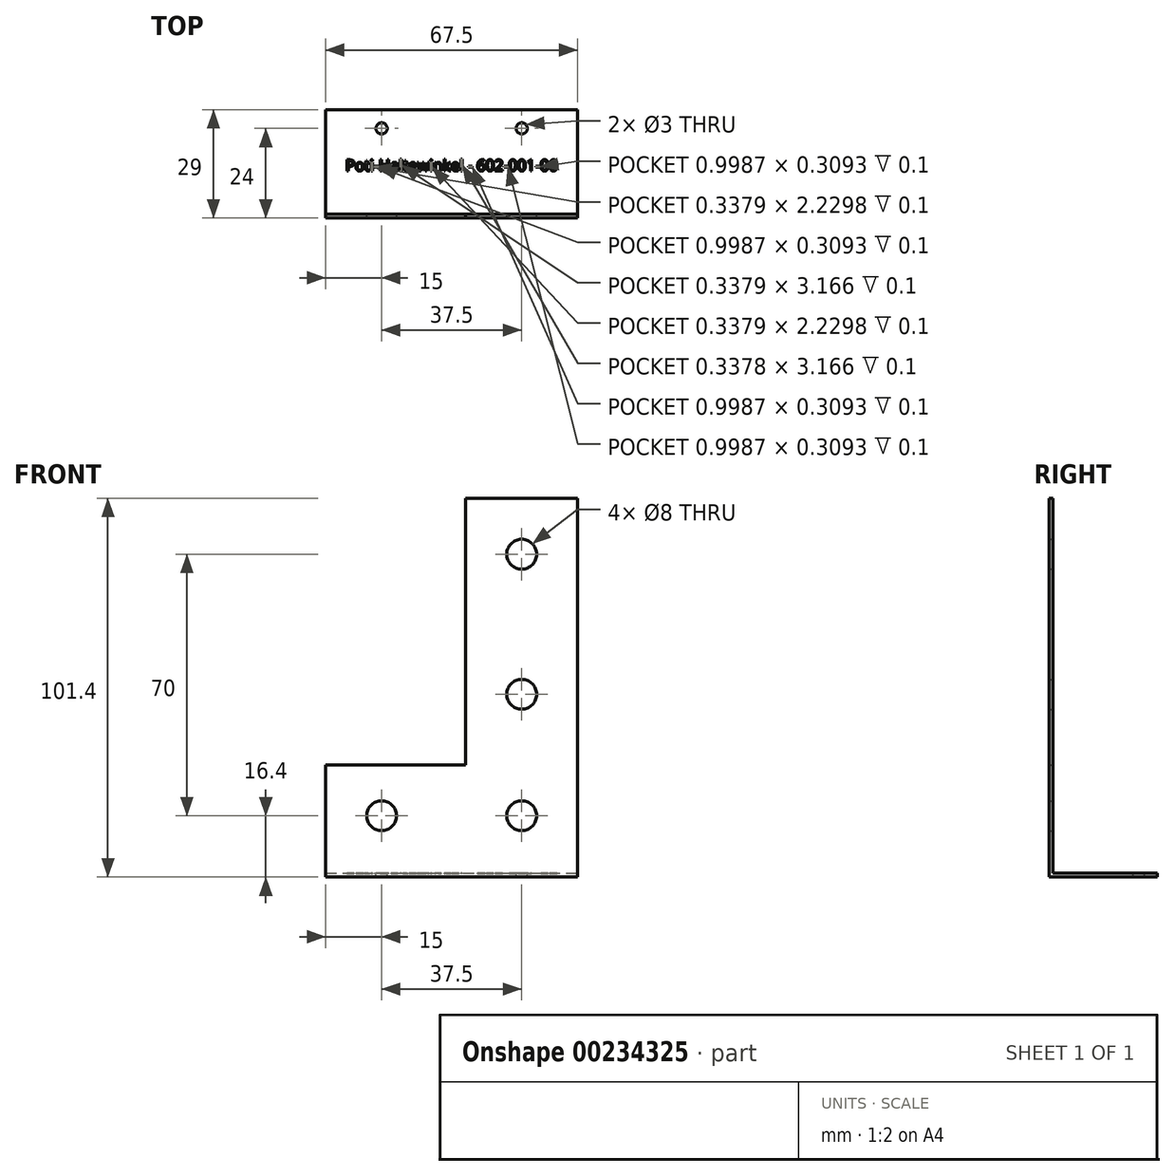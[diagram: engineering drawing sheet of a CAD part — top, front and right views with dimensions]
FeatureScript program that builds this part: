
annotation { "Feature Type Name" : "Feature", "Feature Type Description" : "" }
export const myFeature = defineFeature(function(context is Context, id is Id, definition is map)
    precondition{}
    {
        {
            var Q0;
            Q0=qCreatedBy(makeId("Front.planeOp"),FACE);
            var sketch = newSketch(context, id + "F0", { "sketchPlane" : qUnion([Q0])});
            skLineSegment(sketch, "E0", {"start": v(-37.5, 0) * mm, "end": v(0, 0) * mm});
            skLineSegment(sketch, "E1", {"start": v(0, 0) * mm, "end": v(0, 71.4) * mm});
            skLineSegment(sketch, "E2", {"start": v(0, 71.4) * mm, "end": v(30, 71.4) * mm});
            skLineSegment(sketch, "E3", {"start": v(30, 71.4) * mm, "end": v(30, -30) * mm});
            skLineSegment(sketch, "E4", {"start": v(30, -30) * mm, "end": v(-37.5, -30) * mm});
            skLineSegment(sketch, "E5", {"start": v(-37.5, -30) * mm, "end": v(-37.5, 0) * mm});
            skCircle(sketch, "E6", {"center": v(15, 56.4) * mm, "radius": 4 * mm});
            skPoint(sketch, "E6.centerSnap0", {"position": v(15, 71.4) * mm});
            skCircle(sketch, "E7", {"center": v(15, 18.9) * mm, "radius": 4 * mm});
            skCircle(sketch, "E8", {"center": v(-22.5, -13.6) * mm, "radius": 4 * mm});
            skPoint(sketch, "E9", {"position": v(-37.5, -15) * mm});
            skCircle(sketch, "E10", {"center": v(15, -13.6) * mm, "radius": 4 * mm});
            skLineSegment(sketch, "E11", {"start": v(-37.5, -29) * mm, "end": v(30, -29) * mm});
            skLineSegment(sketch, "E12", {"start": v(-22.5, -13.6) * mm, "end": v(-22.5, -30) * mm, "construction": true});
            skLineSegment(sketch, "E13", {"start": v(15, -13.6) * mm, "end": v(15, -30) * mm, "construction": true});
            skSolve(sketch);
        }
        {
            var Q0;
            Q0=makeQuery(id+"F0.imprint","IMPRINT",FACE,{"disambiguationData":[TD([[makeQuery(id+"F0.imprint","IMPRINT",EDGE,{"derivedFrom":sQuery(id+"F0.wireOp",EDGE,"E0")}),-1.0]])]});
            var Q1;
            {var subQ0=sQuery(id+"F0.wireOp",EDGE,"E4");Q1=makeQuery(id+"F0.imprint","IMPRINT",FACE,{"disambiguationData":[TD([[makeQuery(id+"F0.imprint","IMPRINT",EDGE,{"derivedFrom":subQ0}),-1.0]])]});}
            extrude(context, id + "F1", {"entities" : qUnion([Q0, Q1]), "depth" : 1 * mm});
        }
        {
            var Q0;
            {var subQ0=sQuery(id+"F0.wireOp",EDGE,"E4");Q0=makeQuery(id+"F0.imprint","IMPRINT",FACE,{"disambiguationData":[TD([[makeQuery(id+"F0.imprint","IMPRINT",EDGE,{"derivedFrom":subQ0}),-1.0]])]});}
            extrude(context, id + "F2", {"entities" : qUnion([Q0]), "operationType" : NewBodyOperationType.ADD, "oppositeDirection" : true, "depth" : 28 * mm});
        }
        {
            var Q0;
            Q0=makeQuery(id+"F2.opExtrude","SWEPT_FACE",FACE,{"disambiguationData":[OSD([sQuery(id+"F0.wireOp",EDGE,"E11")])]});
            var sketch = newSketch(context, id + "F3", { "sketchPlane" : qUnion([Q0])});
            skLineSegment(sketch, "E14", {"start": v(15, 0) * mm, "end": v(15, 28) * mm, "construction": true});
            skLineSegment(sketch, "E15", {"start": v(-22.5, 0) * mm, "end": v(-22.5, 28) * mm, "construction": true});
            skCircle(sketch, "E16", {"center": v(15, 23) * mm, "radius": 1.5 * mm});
            skCircle(sketch, "E17", {"center": v(-22.5, 23) * mm, "radius": 1.5 * mm});
            skSolve(sketch);
        }
        {
            var Q0;
            Q0=makeQuery(id+"F3.imprint","IMPRINT",FACE,{"disambiguationData":[TD([[makeQuery(id+"F3.imprint","IMPRINT",EDGE,{"derivedFrom":sQuery(id+"F3.wireOp",EDGE,"E17")}),1.0]])]});
            var Q1;
            Q1=makeQuery(id+"F3.imprint","IMPRINT",FACE,{"disambiguationData":[TD([[makeQuery(id+"F3.imprint","IMPRINT",EDGE,{"derivedFrom":sQuery(id+"F3.wireOp",EDGE,"E16")}),1.0]])]});
            extrude(context, id + "F4", {"entities" : qUnion([Q0, Q1]), "operationType" : NewBodyOperationType.REMOVE, "endBound" : BoundingType.UP_TO_NEXT, "oppositeDirection" : true, "depth" : 25 * mm});
        }
        {
            var Q0;
            Q0=makeQuery(id+"F2.opExtrude","SWEPT_FACE",FACE,{"disambiguationData":[OSD([sQuery(id+"F0.wireOp",EDGE,"E11")])]});
            var sketch = newSketch(context, id + "F5", { "sketchPlane" : qUnion([Q0])});
            skText(sketch, "E18", { "text": "Poti-Haltewinkel - 602-001-00", "fontName": "OpenSans-Regular.ttf"});
            const initialGuessF5  = {"E18": [-0.03214, 0.01161, 1, 0, 0.003]};
            skSetInitialGuess(sketch, initialGuessF5);
            skSolve(sketch);
        }
        {
            var Q0;
            Q0 = qSketchRegion(id + "F5", true);
            extrude(context, id + "F6", {"entities" : qUnion([Q0]), "operationType" : NewBodyOperationType.REMOVE, "oppositeDirection" : true, "depth" : .1 * mm});
        }
    });
